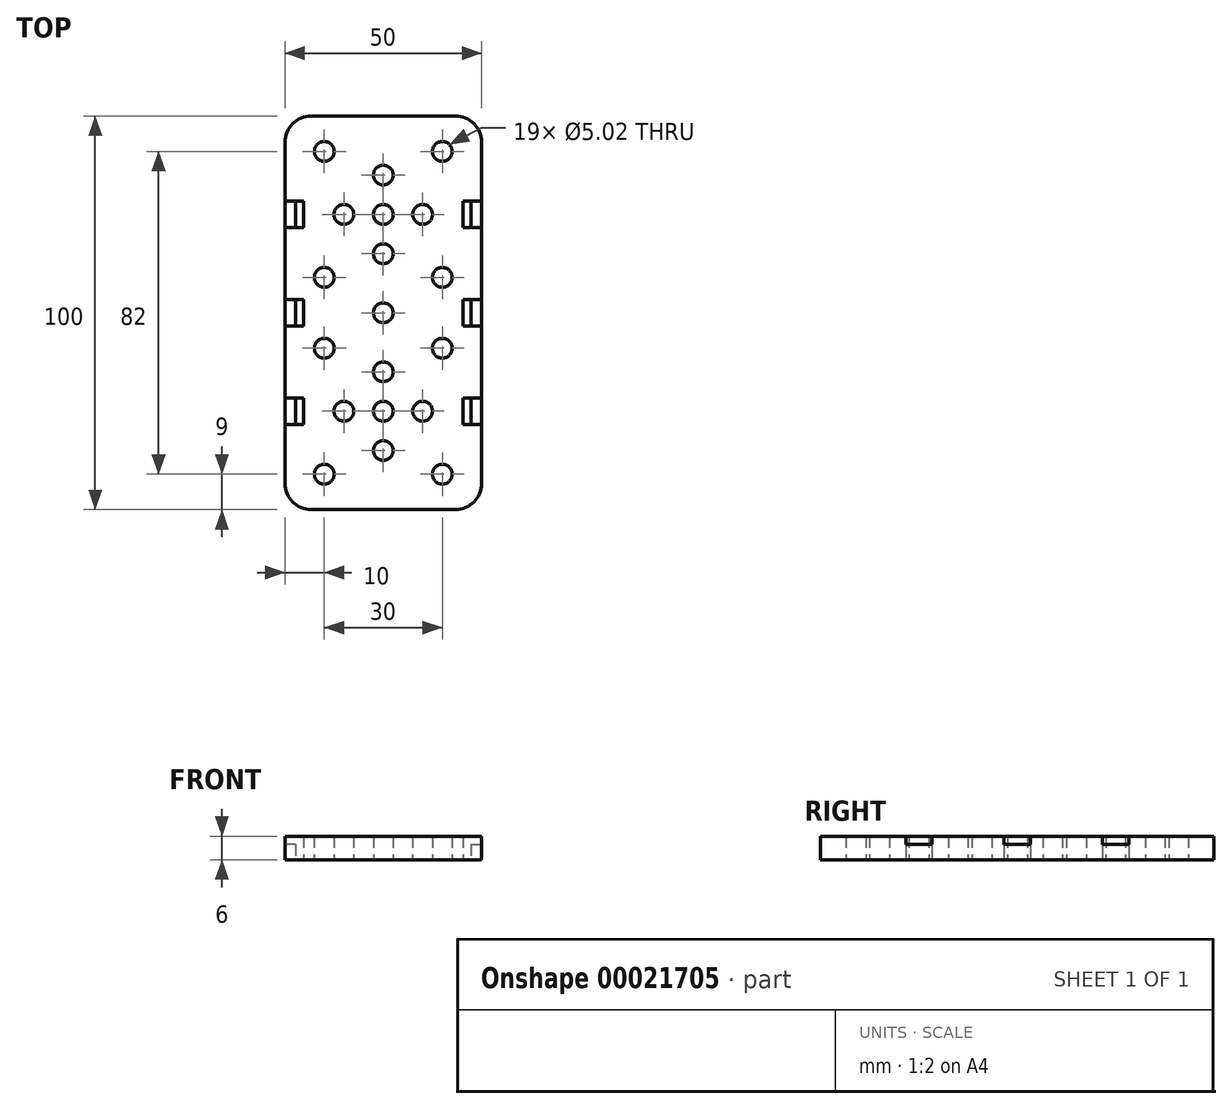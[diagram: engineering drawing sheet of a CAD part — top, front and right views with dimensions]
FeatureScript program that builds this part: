
annotation { "Feature Type Name" : "Feature", "Feature Type Description" : "" }
export const myFeature = defineFeature(function(context is Context, id is Id, definition is map)
    precondition{}
    {
        {
            var Q0;
            Q0=qCreatedBy(makeId("Top.planeOp"),FACE);
            var sketch = newSketch(context, id + "F1", { "sketchPlane" : qUnion([Q0])});
            skLineSegment(sketch, "E0", {"start": v(0, 0) * mm, "end": v(0, 25) * mm, "construction": true});
            skLineSegment(sketch, "E1", {"start": v(0, 0) * mm, "end": v(25, 0) * mm, "construction": true});
            skLineSegment(sketch, "E2", {"start": v(25, 0) * mm, "end": v(25, 18.3) * mm});
            skLineSegment(sketch, "E3", {"start": v(18.3, 25) * mm, "end": v(0, 25) * mm});
            skCircle(sketch, "E4", {"center": v(0, 0) * mm, "radius": 2.5 * mm, "construction": true});
            skLineSegment(sketch, "E5", {"start": v(15, 0) * mm, "end": v(15, 16) * mm, "construction": true});
            skLineSegment(sketch, "E6", {"start": v(15, 16) * mm, "end": v(0, 16) * mm, "construction": true});
            skCircle(sketch, "E7", {"center": v(15, 16) * mm, "radius": 2.5 * mm});
            skPoint(sketch, "E8.visualSharp", {"position": v(25, 25) * mm});
            skArc(sketch, "E8.filletArc", {"start": v(25, 18.3) * mm, "mid": v(23.04, 23.04) * mm, "end": v(18.3, 25) * mm});
            skLineSegment(sketch, "E9", {"start": v(22.26, 0) * mm, "end": v(22.26, 3.35) * mm});
            skLineSegment(sketch, "E10", {"start": v(22.26, 3.35) * mm, "end": v(25, 3.35) * mm});
            skLineSegment(sketch, "E11", {"start": v(22.26, 3.35) * mm, "end": v(20.26, 3.35) * mm});
            skLineSegment(sketch, "E12", {"start": v(20.26, 3.35) * mm, "end": v(20.26, 0) * mm});
            skCircle(sketch, "E13", {"center": v(10, 0) * mm, "radius": 2.5 * mm, "construction": true});
            skCircle(sketch, "E14", {"center": v(0, 10) * mm, "radius": 2.5 * mm, "construction": true});
            skLineSegment(sketch, "E15", {"start": v(10, 0) * mm, "end": v(0, 0) * mm, "construction": true});
            skLineSegment(sketch, "E16", {"start": v(0, 10) * mm, "end": v(0, 0) * mm, "construction": true});
            skArc(sketch, "E17", {"start": v(2.5, 0) * mm, "mid": v(1.77, 1.77) * mm, "end": v(0, 2.5) * mm});
            skArc(sketch, "E18", {"start": v(12.5, 0) * mm, "mid": v(10, 2.51) * mm, "end": v(7.5, 0) * mm});
            skArc(sketch, "E19", {"start": v(0, 7.5) * mm, "mid": v(2.5, 10) * mm, "end": v(0, 12.5) * mm});
            skArc(sketch, "E20.MirrorCS", {"start": v(0, 7.5) * mm, "mid": v(-2.5, 10) * mm, "end": v(0, 12.5) * mm});
            skArc(sketch, "E21.MirrorCS", {"start": v(-2.5, 0) * mm, "mid": v(-1.77, 1.77) * mm, "end": v(0, 2.5) * mm});
            skArc(sketch, "E22.MirrorCS", {"start": v(-12.5, 0) * mm, "mid": v(-10, 2.51) * mm, "end": v(-7.5, 0) * mm});
            skLineSegment(sketch, "E23.MirrorCS", {"start": v(-18.3, 25) * mm, "end": v(0, 25) * mm});
            skArc(sketch, "E24.MirrorCS", {"start": v(-25, 18.3) * mm, "mid": v(-23.04, 23.04) * mm, "end": v(-18.3, 25) * mm});
            skLineSegment(sketch, "E25.MirrorCS", {"start": v(-25, 0) * mm, "end": v(-25, 18.3) * mm});
            skLineSegment(sketch, "E26.MirrorCS", {"start": v(-22.26, 3.35) * mm, "end": v(-25, 3.35) * mm});
            skLineSegment(sketch, "E27.MirrorCS", {"start": v(-22.26, 0) * mm, "end": v(-22.26, 3.35) * mm});
            skLineSegment(sketch, "E28.MirrorCS", {"start": v(-22.26, 3.35) * mm, "end": v(-20.26, 3.35) * mm});
            skLineSegment(sketch, "E29.MirrorCS", {"start": v(-20.26, 3.35) * mm, "end": v(-20.26, 0) * mm});
            skCircle(sketch, "E30.MirrorC", {"center": v(-15, 16) * mm, "radius": 2.5 * mm});
            skLineSegment(sketch, "E31.MirrorCS", {"start": v(-25, 0) * mm, "end": v(-25, -25) * mm});
            skLineSegment(sketch, "E32.MirrorCS", {"start": v(-22.26, -3.35) * mm, "end": v(-25, -3.35) * mm});
            skLineSegment(sketch, "E33.MirrorCS", {"start": v(-22.26, 0) * mm, "end": v(-22.26, -3.35) * mm});
            skLineSegment(sketch, "E34.MirrorCS", {"start": v(-20.26, -3.35) * mm, "end": v(-20.26, 0) * mm});
            skLineSegment(sketch, "E35.MirrorCS", {"start": v(-22.26, -3.35) * mm, "end": v(-20.26, -3.35) * mm});
            skArc(sketch, "E36.MirrorCS", {"start": v(-12.5, 0) * mm, "mid": v(-10, -2.51) * mm, "end": v(-7.5, 0) * mm});
            skCircle(sketch, "E37.MirrorC", {"center": v(-15, -16) * mm, "radius": 2.5 * mm});
            skLineSegment(sketch, "E38.MirrorCS", {"start": v(-25, -25) * mm, "end": v(0, -25) * mm, "construction": true});
            skArc(sketch, "E39.MirrorCS", {"start": v(-2.5, 0) * mm, "mid": v(-1.77, -1.77) * mm, "end": v(0, -2.5) * mm});
            skArc(sketch, "E40.MirrorCS", {"start": v(2.5, 0) * mm, "mid": v(1.77, -1.77) * mm, "end": v(0, -2.5) * mm});
            skArc(sketch, "E41.MirrorCS", {"start": v(0, -7.5) * mm, "mid": v(2.5, -10) * mm, "end": v(0, -12.5) * mm});
            skArc(sketch, "E42.MirrorCS", {"start": v(0, -7.5) * mm, "mid": v(-2.5, -10) * mm, "end": v(0, -12.5) * mm});
            skArc(sketch, "E43.MirrorCS", {"start": v(12.5, 0) * mm, "mid": v(10, -2.51) * mm, "end": v(7.5, 0) * mm});
            skCircle(sketch, "E44.MirrorC", {"center": v(15, -16) * mm, "radius": 2.5 * mm});
            skLineSegment(sketch, "E45.MirrorCS", {"start": v(25, -25) * mm, "end": v(0, -25) * mm, "construction": true});
            skLineSegment(sketch, "E46.MirrorCS", {"start": v(25, 0) * mm, "end": v(25, -25) * mm});
            skLineSegment(sketch, "E47.MirrorCS", {"start": v(20.26, -3.35) * mm, "end": v(20.26, 0) * mm});
            skLineSegment(sketch, "E48.MirrorCS", {"start": v(22.26, -3.35) * mm, "end": v(20.26, -3.35) * mm});
            skLineSegment(sketch, "E49.MirrorCS", {"start": v(22.26, 0) * mm, "end": v(22.26, -3.35) * mm});
            skLineSegment(sketch, "E50.MirrorCS", {"start": v(22.26, -3.35) * mm, "end": v(25, -3.35) * mm});
            skPoint(sketch, "E51.orphan", {"position": v(-25, -18.3) * mm});
            skPoint(sketch, "E52.orphan", {"position": v(25, -18.3) * mm});
            skPoint(sketch, "E53.orphan", {"position": v(-18.3, -25) * mm});
            skPoint(sketch, "E54.orphan", {"position": v(18.3, -25) * mm});
            skLineSegment(sketch, "E55.MirrorCS", {"start": v(-22.25, -46.65) * mm, "end": v(-20.25, -46.65) * mm});
            skLineSegment(sketch, "E56.MirrorCS", {"start": v(22.26, -53.35) * mm, "end": v(20.26, -53.35) * mm});
            skLineSegment(sketch, "E57.MirrorCS", {"start": v(22.26, -46.65) * mm, "end": v(20.26, -46.65) * mm});
            skLineSegment(sketch, "E58.MirrorCS", {"start": v(22.26, -50) * mm, "end": v(22.26, -53.35) * mm});
            skLineSegment(sketch, "E59.MirrorCS", {"start": v(-20.25, -46.65) * mm, "end": v(-20.25, -50) * mm});
            skLineSegment(sketch, "E60.MirrorCS", {"start": v(20.26, -53.35) * mm, "end": v(20.26, -50) * mm});
            skLineSegment(sketch, "E61.MirrorCS", {"start": v(-22.25, -50) * mm, "end": v(-22.25, -53.35) * mm});
            skLineSegment(sketch, "E62.MirrorCS", {"start": v(-20.25, -53.35) * mm, "end": v(-20.25, -50) * mm});
            skLineSegment(sketch, "E63.MirrorCS", {"start": v(-22.25, -53.35) * mm, "end": v(-20.25, -53.35) * mm});
            skArc(sketch, "E64.MirrorCS", {"start": v(2.51, -50) * mm, "mid": v(1.77, -48.23) * mm, "end": v(0, -47.49) * mm});
            skLineSegment(sketch, "E65.MirrorCS", {"start": v(22.26, -50) * mm, "end": v(22.26, -46.65) * mm});
            skLineSegment(sketch, "E66.MirrorCS", {"start": v(-22.25, -50) * mm, "end": v(-22.25, -46.65) * mm});
            skLineSegment(sketch, "E67.MirrorCS", {"start": v(20.26, -46.65) * mm, "end": v(20.26, -50) * mm});
            skCircle(sketch, "E68.MirrorC", {"center": v(10, -50) * mm, "radius": 2.5 * mm});
            skCircle(sketch, "E69.MirrorC", {"center": v(0, -60) * mm, "radius": 2.5 * mm});
            skLineSegment(sketch, "E70.MirrorCS", {"start": v(10, -50) * mm, "end": v(0, -50) * mm, "construction": true});
            skCircle(sketch, "E71.MirrorC", {"center": v(0, -50) * mm, "radius": 2.5 * mm});
            skLineSegment(sketch, "E72.MirrorCS", {"start": v(22.26, -53.35) * mm, "end": v(25, -53.35) * mm});
            skLineSegment(sketch, "E73.MirrorCS", {"start": v(22.26, -46.65) * mm, "end": v(25, -46.65) * mm});
            skArc(sketch, "E74.MirrorCS", {"start": v(-2.5, -50) * mm, "mid": v(-1.77, -48.23) * mm, "end": v(0, -47.49) * mm});
            skLineSegment(sketch, "E75.MirrorCS", {"start": v(-22.25, -53.35) * mm, "end": v(-25, -53.35) * mm});
            skLineSegment(sketch, "E76.MirrorCS", {"start": v(-22.25, -46.65) * mm, "end": v(-25, -46.65) * mm});
            skArc(sketch, "E77.MirrorCS", {"start": v(0, -42.5) * mm, "mid": v(-2.5, -40) * mm, "end": v(0, -37.49) * mm});
            skArc(sketch, "E78.MirrorCS", {"start": v(0, -57.49) * mm, "mid": v(2.51, -60) * mm, "end": v(0, -62.5) * mm});
            skPoint(sketch, "E79.MirrorP", {"position": v(25, -75) * mm});
            skLineSegment(sketch, "E80.MirrorCS", {"start": v(0, -50) * mm, "end": v(0, -75) * mm, "construction": true});
            skLineSegment(sketch, "E81.MirrorCS", {"start": v(0, -50) * mm, "end": v(25, -50) * mm, "construction": true});
            skLineSegment(sketch, "E82.MirrorCS", {"start": v(25, -50) * mm, "end": v(25, -68.3) * mm});
            skLineSegment(sketch, "E83.MirrorCS", {"start": v(18.3, -75) * mm, "end": v(0, -75) * mm});
            skLineSegment(sketch, "E84.MirrorCS", {"start": v(15, -50) * mm, "end": v(15, -66) * mm, "construction": true});
            skLineSegment(sketch, "E85.MirrorCS", {"start": v(15, -66) * mm, "end": v(0, -66) * mm, "construction": true});
            skCircle(sketch, "E86.MirrorC", {"center": v(15, -66) * mm, "radius": 2.5 * mm});
            skArc(sketch, "E87.MirrorCS", {"start": v(25, -68.3) * mm, "mid": v(23.04, -73.04) * mm, "end": v(18.3, -75) * mm});
            skArc(sketch, "E88.MirrorCS", {"start": v(12.51, -50) * mm, "mid": v(10, -47.49) * mm, "end": v(7.5, -50) * mm});
            skLineSegment(sketch, "E89.MirrorCS", {"start": v(-18.3, -75) * mm, "end": v(0, -75) * mm});
            skArc(sketch, "E90.MirrorCS", {"start": v(0, -57.49) * mm, "mid": v(-2.5, -60) * mm, "end": v(0, -62.5) * mm});
            skArc(sketch, "E91.MirrorCS", {"start": v(-12.5, -50) * mm, "mid": v(-10, -47.49) * mm, "end": v(-7.49, -50) * mm});
            skLineSegment(sketch, "E92.MirrorCS", {"start": v(0, -60) * mm, "end": v(0, -50) * mm, "construction": true});
            skPoint(sketch, "E93.MirrorP", {"position": v(-25, -31.7) * mm});
            skCircle(sketch, "E94.MirrorC", {"center": v(15, -34) * mm, "radius": 2.5 * mm});
            skArc(sketch, "E95.MirrorCS", {"start": v(-25, -68.3) * mm, "mid": v(-23.04, -73.04) * mm, "end": v(-18.3, -75) * mm});
            skArc(sketch, "E96.MirrorCS", {"start": v(-2.5, -50) * mm, "mid": v(-1.77, -51.77) * mm, "end": v(0, -52.5) * mm});
            skCircle(sketch, "E97.MirrorC", {"center": v(-15, -34) * mm, "radius": 2.5 * mm});
            skCircle(sketch, "E98.MirrorC", {"center": v(-15, -66) * mm, "radius": 2.5 * mm});
            skLineSegment(sketch, "E99.MirrorCS", {"start": v(25, -50) * mm, "end": v(25, -25) * mm});
            skArc(sketch, "E100.MirrorCS", {"start": v(2.51, -50) * mm, "mid": v(1.77, -51.77) * mm, "end": v(0, -52.5) * mm});
            skPoint(sketch, "E101.MirrorP", {"position": v(25, -31.7) * mm});
            skArc(sketch, "E102.MirrorCS", {"start": v(0, -42.5) * mm, "mid": v(2.51, -40) * mm, "end": v(0, -37.49) * mm});
            skLineSegment(sketch, "E103.MirrorCS", {"start": v(-25, -50) * mm, "end": v(-25, -68.3) * mm});
            skArc(sketch, "E104.MirrorCS", {"start": v(-12.5, -50) * mm, "mid": v(-10, -52.5) * mm, "end": v(-7.49, -50) * mm});
            skLineSegment(sketch, "E105.MirrorCS", {"start": v(-25, -50) * mm, "end": v(-25, -25) * mm});
            skArc(sketch, "E106.MirrorCS", {"start": v(12.51, -50) * mm, "mid": v(10, -52.5) * mm, "end": v(7.5, -50) * mm});
            skLineSegment(sketch, "E107", {"start": v(22.26, -25) * mm, "end": v(22.26, -21.65) * mm});
            skLineSegment(sketch, "E108", {"start": v(22.26, -21.65) * mm, "end": v(25, -21.65) * mm});
            skLineSegment(sketch, "E109", {"start": v(22.26, -21.65) * mm, "end": v(20.26, -21.65) * mm});
            skLineSegment(sketch, "E110", {"start": v(20.26, -21.65) * mm, "end": v(20.26, -25) * mm});
            skLineSegment(sketch, "E111.MirrorCS", {"start": v(22.26, -28.35) * mm, "end": v(25, -28.35) * mm});
            skLineSegment(sketch, "E112.MirrorCS", {"start": v(22.26, -28.35) * mm, "end": v(20.26, -28.35) * mm});
            skLineSegment(sketch, "E113.MirrorCS", {"start": v(20.26, -28.35) * mm, "end": v(20.26, -25) * mm});
            skLineSegment(sketch, "E114.MirrorCS", {"start": v(22.26, -25) * mm, "end": v(22.26, -28.35) * mm});
            skLineSegment(sketch, "E115.MirrorCS", {"start": v(-20.26, -21.65) * mm, "end": v(-20.26, -25) * mm});
            skLineSegment(sketch, "E116.MirrorCS", {"start": v(-22.26, -21.65) * mm, "end": v(-20.26, -21.65) * mm});
            skLineSegment(sketch, "E117.MirrorCS", {"start": v(-22.26, -25) * mm, "end": v(-22.26, -21.65) * mm});
            skLineSegment(sketch, "E118.MirrorCS", {"start": v(-22.26, -21.65) * mm, "end": v(-25, -21.65) * mm});
            skLineSegment(sketch, "E119.MirrorCS", {"start": v(-22.26, -28.35) * mm, "end": v(-25, -28.35) * mm});
            skLineSegment(sketch, "E120.MirrorCS", {"start": v(-22.26, -28.35) * mm, "end": v(-20.26, -28.35) * mm});
            skLineSegment(sketch, "E121.MirrorCS", {"start": v(-20.25, -28.35) * mm, "end": v(-20.25, -25) * mm});
            skLineSegment(sketch, "E122.MirrorCS", {"start": v(-22.26, -25) * mm, "end": v(-22.26, -28.35) * mm});
            skCircle(sketch, "E123", {"center": v(0, -25) * mm, "radius": 2.51 * mm});
            skSolve(sketch);
        }
        {
            var Q0;
            Q0=makeQuery(id+"F1.imprint","IMPRINT",FACE,{"disambiguationData":[TD([[makeQuery(id+"F1.imprint","IMPRINT",EDGE,{"derivedFrom":sQuery(id+"F1.wireOp",EDGE,"E3")}),1.0]])]});
            extrude(context, id + "F0", {"entities" : qUnion([Q0]), "depth" : 6 * mm});
        }
        {
            var Q0;
            {var subQ4=sQuery(id+"F1.wireOp",EDGE,"E26.MirrorCS");Q0=makeQuery(id+"F1.imprint","IMPRINT",FACE,{"disambiguationData":[TD([[makeQuery(id+"F1.imprint","IMPRINT",EDGE,{"derivedFrom":subQ4}),1.0]])]});}
            var Q1;
            Q1=makeQuery(id+"F1.imprint","IMPRINT",FACE,{"disambiguationData":[TD([[makeQuery(id+"F1.imprint","IMPRINT",EDGE,{"derivedFrom":sQuery(id+"F1.wireOp",EDGE,"E9")}),-1.0]])]});
            var Q2;
            Q2=makeQuery(id+"F1.imprint","IMPRINT",FACE,{"disambiguationData":[TD([[makeQuery(id+"F1.imprint","IMPRINT",EDGE,{"derivedFrom":sQuery(id+"F1.wireOp",EDGE,"E61.MirrorCS")}),-1.0]])]});
            var Q3;
            Q3=makeQuery(id+"F1.imprint","IMPRINT",FACE,{"disambiguationData":[TD([[makeQuery(id+"F1.imprint","IMPRINT",EDGE,{"derivedFrom":sQuery(id+"F1.wireOp",EDGE,"E58.MirrorCS")}),1.0]])]});
            var Q4;
            Q4=makeQuery(id+"F1.imprint","IMPRINT",FACE,{"disambiguationData":[TD([[makeQuery(id+"F1.imprint","IMPRINT",EDGE,{"derivedFrom":sQuery(id+"F1.wireOp",EDGE,"E117.MirrorCS")}),1.0]])]});
            var Q5;
            Q5=makeQuery(id+"F1.imprint","IMPRINT",FACE,{"disambiguationData":[TD([[makeQuery(id+"F1.imprint","IMPRINT",EDGE,{"derivedFrom":sQuery(id+"F1.wireOp",EDGE,"E107")}),-1.0]])]});
            extrude(context, id + "F2", {"entities" : qUnion([Q0, Q1, Q2, Q3, Q4, Q5]), "operationType" : NewBodyOperationType.ADD, "depth" : 4 * mm});
        }
    });
